# Revit family: IS_CerathermC100_A6956_BIM_NL
name_source: partatom
category: Plumbing Fixtures
units: mm (PartAtom-declared; Revit-internal decimal feet)

## family parameters
Always vertical = No
Cut with Voids When Loaded = No
OmniClass Number = 23.45.55.17
OmniClass Title = Mixing Faucets
Part Type = Normal
Room Calculation Point = No
Round Connector Dimension = Use Diameter
Shared = No
Work Plane-Based = No

## types (5) — shared parameters
Accesoires = https://www.idealstandard.nl
Accessories = https://www.idealstandard.nl
Afmetingen = 163 x 79 x 163 mm
AfstandsEenheid = Millimeter
AreaUnits = Millimetres
Artikelomschrijving = CERATHERM C100 THERMOSTATISCHE DUSCHE EINBAUSATZ2/EASY-BUILT
Artikelreferentie = CERATHERM C100 THERMOSTATIC SHOWER BUILT-IN KIT2/EASY-BUILT
Auteur = Ideal Standard
BIMObjectName = IS_IdealStandard_Showermixers_CerathermC100_A6956
BIMobject category = Sanitary
BIMobject category code = Taps & Mixers
BIMobject main category = Sanitary
Bedieningkraan = Handbuch
Bedieningkraanwerk = drehen wissen
Beschrijvingdouchekop = Regenbrause
Beschrijvinggarantie = Herstellergarantie
BimObjectNaam = IS_IdealStandard_Showermixers_CerathermC100_A6956
Brand = Ideal Standard
Brand url = http://www.idealstandard.nl
Breedte = 163
ConnectionType = Installation
CurrencyUnit = €
CurrentRevision = 1
Date of publishing = 24/07/2021
Diepte = 79 mm
Douchebak = No
DurationUnit = Years
Edition number = 1
FaucetFunction = Mixer
FaucetOperation = Turning Knobs Controless
FaucetType = Thermostatic Mixer
Functieindoucheruimte = Thermostat-Brausemischer
Functiekraanwerk = Thermostat-Brausemischer
Garantieonderdelen = 5
Garantieunits = Jaren
GemaaktOp = 27/07/2021
HasIntegralShutOffDevice = No
Help = https://www.idealstandard.nl
Hoogte = 163.00002
Hulp = https://www.idealstandard.nl
IFC Classification = Sanitary Terminal
IfcExportAs = IfcValveType
IfcExportType = MIXING
Installatieinstructies = https://www.idealstandard.nl
Installation instructions = https://www.idealstandard.nl
InstallationInstructions = https://www.idealstandard.nl
IsBuiltIn = No
IsHighPressure = No
Klepmechanisme = Drehknöpfe Controlless
LinearUnits = Millimetres
MaintenanceInformation = https://www.idealstandard.nl
Manufacturer = Ideal Standard
Manufacturer name = Ideal Standard
ManufacturerURL = https://www.idealstandard.nl
Materiaal = Messing
Material = Brass
Material main = Brass
Merk = Ideal Standard
ModelReference = CERATHERM C100 THERMOSTATIC SHOWER BUILT-IN KIT2/EASY-BUILT
Montageinstuctie = https://www.idealstandard.nl
NBS Reference Code = 45-35-70/335
NBS Reference Description = Shower mixers
Name = Showermixers_CerathermC100_A6956_IdealStandard
NominalDepth = 79 mm
NominalHeight = 163 mm  [stored 0.534777 ft]
NominalLength = 79 mm
NominalWidth = 163 mm  [stored 0.534777 ft]
Normen = Showermixers_CerathermC100_A6956_IdealStandard
OppervlakteEenheid = Millimeter
Product Guid = a7b6b910-f24c-46c9-998a-aebfb8dc873d
Product SKU = A6956
Product certification = https://www.idealstandard.nl
Product data url = https://bimobject.com
Product family = Sanitary
Product group = Showers
Product name = CERATHERM C100 THERMOSTATIC SHOWER BUILT-IN KIT2/EASY-BUILT
Product url = https://www.idealstandard.nl
ProductInformation = https://www.idealstandard.nl
ProductSoort = Sanitary
Productinformatie = https://www.idealstandard.nl
QR code = http://bimobject.com
Referentie = CERATHERM C100 THERMOSTATIC SHOWER BUILT-IN KIT2/EASY-BUILT
Revisie = 1
Shape = Cylindrical
ShowerType = Thermostatic Shower Mixer
Size = 163 x 79 x 163 mm
Space = Internal
SpareParts = https://www.idealstandard.nl
Technical description = https://www.idealstandard.nl
Telefoonnummer = 077 355 08 08
TestPressure = 10 Bar
Testdruk = 10 Bar
Typeconnectie = Installation
URL = https://www.idealstandard.nl
Uniclass 2.0 Code = PR-35-06-82
Uniclass 2.0 Description = Shower Mixer
Uniclass 2015 Code = Pr_40_20_87_80
Uniclass 2015 Name = Shower thermostatic valves
Uniclass2015Beschrijving = Shower thermostatic valves
Uniclass2015Code = Pr_40_20_87_80
Uniclass2015Referentie = Pr_40_20_87_80
Uniclass2015Title = Shower thermostatic valves
Uniclass2015Version = v1.22
Urlproducent = https://www.idealstandard.nl
ValutaEenheid = Euro
Versie = 1
Version = 1
VolumeUnits = Litres
Volumeunits = Liters
Vorm = zylindrisch
WRASURL = https://www.wrasapprovals.co.uk
WarrantyDescription = Manufacturer warranty
WarrantyDurationUnit = Years
Wisselstukken = https://www.idealstandard.nl
Youtube clip = https://www.youtube.com
zero-valued in all types: BrutoGewicht, Cost, Lengte, Vervangingskosten

## per-type parameters (varying)
| type | Afwerking | Artikelnummer | BarCode | Barcode | Color | Description | Eigenschappen | Features | Finish | GTIN code | Kleur | MainColor | Model | ModelNumber | NettWeight | Nettogewicht |
| A6956AA - CERATHERM C100 THERMOSTATIC SHOWER BUILT-IN KIT2/EASY-BUILT  - CHROME | Chrom | A6956AA | 4015413350440 | 4015413350440 | Chrom | CERATHERM C100 THERMOSTATISCHE DUSCHE EINBAUSATZ2/EASY-BUILT - CHROM | THERMOSTATISCHE DUSCHE EINBAUSATZ2/EASY-BUILT - CHROM | THERMOSTATISCHE DUSCHE EINBAUSATZ2/EASY-BUILT - CHROM | Chrom | https://4015413350440 | Chrom | Chrom | A6956AA | A6956AA | 1.64 | 1.64 |
| A6956A5 - CERATHERM C100 THERMOSTATIC SHOWER BUILT-IN KIT2/EASY-BUILT  - MAGNETIC GREY | magnetisch grau | A6956A5 | 4015413350457 | 4015413350457 | magnetisch grau | CERATHERM C100 THERMOSTATISCHE DUSCHE EINBAUSATZ2/EASY-BUILT - MAGNETISCHES GRAU | THERMOSTATISCHE DUSCHE EINBAUSATZ2/EASY-BUILT - MAGNETISCHES GRAU | THERMOSTATISCHE DUSCHE EINBAUSATZ2/EASY-BUILT - MAGNETISCHES GRAU | magnetisch grau | https://4015413350457 | magnetisch grau | magnetisch grau | A6956A5 | A6956A5 | 1.64 | 1.64 |
| A6956XG - CERATHERM C100 THERMOSTATIC SHOWER BUILT-IN KIT2/EASY-BUILT  - SILK BLACK | Seide schwarz | A6956XG | 4015413350624 | 4015413350624 | Seide schwarz | CERATHERM C100 THERMOSTATISCHE DUSCHE EINBAUSATZ2/EASY-BUILT - SEIDE SCHWARZ | THERMOSTATISCHE DUSCHE EINBAUSATZ2/EASY-BUILT - SEIDE SCHWARZ | THERMOSTATISCHE DUSCHE EINBAUSATZ2/EASY-BUILT - SEIDE SCHWARZ | Seide schwarz | https://4015413350624 | Seide schwarz | Seide schwarz | A6956XG | A6956XG | 1.64 | 1.64 |
| A6956GN - CERATHERM C100 THERMOSTATIC SHOWER BUILT-IN KIT2/EASY-BUILT  - SILVER STORM | silberner Sturm | A6956GN | 4015413350433 | 4015413350433 | silberner Sturm | CERATHERM C100 THERMOSTATISCHE DUSCHE EINBAUSATZ2/EASY-BUILT - SILBER STURM | THERMOSTATISCHE DUSCHE EINBAUSATZ2/EASY-BUILT - SILBER STURM | THERMOSTATISCHE DUSCHE EINBAUSATZ2/EASY-BUILT - SILBER STURM | silberner Sturm | https://4015413350433 | silberner Sturm | silberner Sturm | A6956GN | A6956GN | 1.86 | 1.86 |
| A6956A2 - CERATHERM C100 THERMOSTATIC SHOWER BUILT-IN KIT2/EASY-BUILT  - BRUSH GOLD | Pinsel gold | A6956A2 | 4015413350464 | 4015413350464 | Pinsel gold | CERATHERM C100 THERMOSTATISCHE DUSCHE EINBAUSATZ2/EASY-BUILT - PINSEL GOLD | THERMOSTATISCHE DUSCHE EINBAUSATZ2/EASY-BUILT - PINSEL GOLD | THERMOSTATISCHE DUSCHE EINBAUSATZ2/EASY-BUILT - PINSEL GOLD | Pinsel gold | https://4015413350464 | Pinsel gold | Pinsel gold | A6956A2 | A6956A2 | 1.64 | 1.64 |

note: [stored X ft] marks values corroborated as IEEE doubles in the binary element streams (Revit-internal decimal feet)

## geometry (parser evidence)
native form markers: Sweep x4
no freeform markers — native parametric forms only
